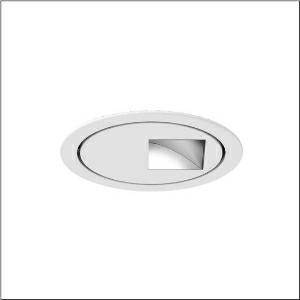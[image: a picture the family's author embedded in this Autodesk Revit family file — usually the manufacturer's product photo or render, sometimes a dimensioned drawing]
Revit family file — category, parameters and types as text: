
# Revit family: lunis_11_mini_round_51dk11cd2wg21
name_source: partatom
category: Lighting Fixtures
units: mm (PartAtom-declared; Revit-internal decimal feet)

## family parameters
Cut with Voids When Loaded = No
Host = Face
Light Source = No
Part Type = Normal
Room Calculation Point = No
Round Connector Dimension = Use Diameter
Shared = No

## types (1)
- Lunis 11 mini round (1 x LED 4000K / CRI = 80 (unbekannt), 2470 lm, 4000K)
    Apparent Load = 28 VA
    CIE Flux Codes = 44 77 97 100 100
    Color Rendering = 80
    Color Temperature = 4000K
    Default Elevation = 1800 mm
    Description = Lunis 11 mini round, downlight, light control with wallwasher, of highly reflective aluminium, highly specular, light emission: direct distribution, LED rated luminous flux: 2.470lm, light colour: 840, control gear: ECG, with terminal, 5-pole, mains connection: 220..230V, AC/DC, 0/50..60Hz, LED module, luminaire module, of aluminium, highly specular, white, diameter: 176mm, clamping range: 1..40mm, recessing ring, of plastic, traffic white (RAL 9016), protection rating (complete): IP20, insulation class (complete): insulation class II (safety insulation), certification: CE, permissible ambient temperature for indoor applications: 0..+35°C, packaging unit: 1 piece
    Height = 0 mm  [stored 0 ft]
    Lamp = 1 x LED 4000K / CRI >= 80 (unbekannt)
    Lamp Light Flux = 2470 lm
    Lamp count = 1
    Length = 176 mm
    Luminous efficacy = 89 lm/W
    Manufacturer = Siteco
    ModVariant = No
    Model = 51DK11CD2WG21
    Mounting Place = Ceiling
    Mounting Type = Recessed
    Number of Poles = 1
    OnlyDefault = Yes
    Power Factor = 1
    Product Name = Lunis 11 mini round
    Product group = downlight
    ProductGroupID = 400
    Protection Class = Protection class II
    Protection Degree = IP 20
    RLX_Detail_Level = 1
    RLX_Emergency_Light_Flux = 0 lm
    RLX_Emergency_Type = 0
    RLX_Emergency_Type_DB = No
    RlxData = <blob elided: 59321 chars, md5=05242995>
    Socket = socket
    Standby Power = 0 W
    System Light Flux = 2470 lm
    System Power = 28 W
    Type Comments = Product without accessories
    Type Image = l_1004772.jpg
    URL = http://relux.com
    VarID = ---
    Voltage = 0 V
    Weight = 0.00 kg
    Width = 176 mm

note: [stored X ft] marks values corroborated as IEEE doubles in the binary element streams (Revit-internal decimal feet)

## geometry (parser evidence)
native form markers: Blend x4, Sweep x11
no freeform markers — native parametric forms only
